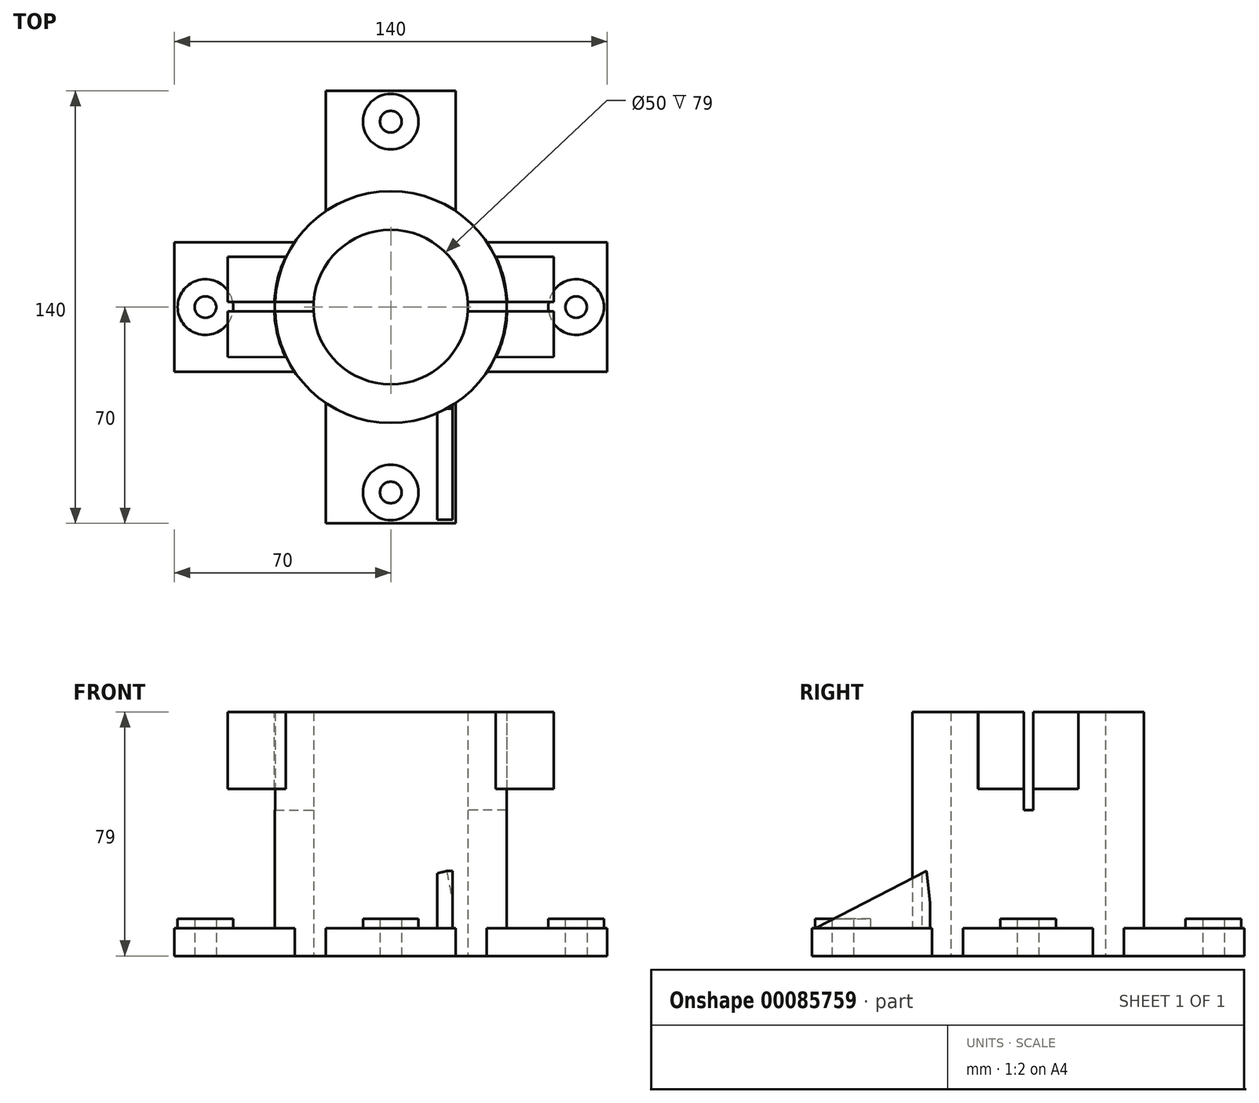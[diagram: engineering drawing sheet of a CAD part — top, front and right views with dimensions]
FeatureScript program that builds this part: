
annotation { "Feature Type Name" : "Feature", "Feature Type Description" : "" }
export const myFeature = defineFeature(function(context is Context, id is Id, definition is map)
    precondition{}
    {
        {
            var Q0;
            Q0=qCreatedBy(makeId("Top.planeOp"),FACE);
            var sketch = newSketch(context, id + "F0", { "sketchPlane" : qUnion([Q0])});
            skCircle(sketch, "E0", {"center": v(0, 0) * mm, "radius": 25 * mm});
            skCircle(sketch, "E1", {"center": v(0, 0) * mm, "radius": 37.5 * mm});
            skSolve(sketch);
        }
        {
            var Q0;
            Q0 = qSketchRegion(id + "F0", true);
            extrude(context, id + "F1", {"entities" : qUnion([Q0]), "depth" : 79 * mm});
        }
        {
            var Q0;
            Q0=qCreatedBy(makeId("Top.planeOp"),FACE);
            var sketch = newSketch(context, id + "F2", { "sketchPlane" : qUnion([Q0])});
            skLineSegment(sketch, "E2", {"start": v(-21, 31.07) * mm, "end": v(-21, 70) * mm});
            skLineSegment(sketch, "E3", {"start": v(21, 31.07) * mm, "end": v(21, 70) * mm});
            skArc(sketch, "E4", {"start": v(-21, 31.07) * mm, "mid": v(0, 37.5) * mm, "end": v(21, 31.07) * mm});
            skLineSegment(sketch, "E5", {"start": v(-21, 70) * mm, "end": v(21, 70) * mm});
            skPoint(sketch, "E6.center", {"position": v(0, -1.43) * mm});
            skLineSegment(sketch, "E7.1.0", {"start": v(-31.07, -21) * mm, "end": v(-70, -21) * mm});
            skLineSegment(sketch, "E7.1.1", {"start": v(-70, -21) * mm, "end": v(-70, 21) * mm});
            skLineSegment(sketch, "E7.1.2", {"start": v(-31.07, 21) * mm, "end": v(-70, 21) * mm});
            skArc(sketch, "E7.1.3", {"start": v(-31.07, -21) * mm, "mid": v(-37.5, 0) * mm, "end": v(-31.07, 21) * mm});
            skLineSegment(sketch, "E7.2.0", {"start": v(21, -31.07) * mm, "end": v(21, -70) * mm});
            skLineSegment(sketch, "E7.2.1", {"start": v(21, -70) * mm, "end": v(-21, -70) * mm});
            skLineSegment(sketch, "E7.2.2", {"start": v(-21, -31.07) * mm, "end": v(-21, -70) * mm});
            skArc(sketch, "E7.2.3", {"start": v(21, -31.07) * mm, "mid": v(0, -37.5) * mm, "end": v(-21, -31.07) * mm});
            skLineSegment(sketch, "E7.3.0", {"start": v(31.07, 21) * mm, "end": v(70, 21) * mm});
            skLineSegment(sketch, "E7.3.1", {"start": v(70, 21) * mm, "end": v(70, -21) * mm});
            skLineSegment(sketch, "E7.3.2", {"start": v(31.07, -21) * mm, "end": v(70, -21) * mm});
            skArc(sketch, "E7.3.3", {"start": v(31.07, 21) * mm, "mid": v(37.5, 0) * mm, "end": v(31.07, -21) * mm});
            skSolve(sketch);
        }
        {
            var Q0;
            Q0 = qSketchRegion(id + "F2", true);
            extrude(context, id + "F3", {"entities" : qUnion([Q0]), "operationType" : NewBodyOperationType.ADD, "depth" : 9 * mm});
        }
        {
            var Q0;
            Q0=qCreatedBy(makeId("Top.planeOp"),FACE);
            var sketch = newSketch(context, id + "F4", { "sketchPlane" : qUnion([Q0])});
            skCircle(sketch, "E8", {"center": v(-60, 0) * mm, "radius": 4 * mm});
            skCircle(sketch, "E9.1.0", {"center": v(0, -60) * mm, "radius": 4 * mm});
            skCircle(sketch, "E9.2.0", {"center": v(60, 0) * mm, "radius": 4 * mm});
            skCircle(sketch, "E9.3.0", {"center": v(0, 60) * mm, "radius": 4 * mm});
            skPoint(sketch, "E9.center", {"position": v(0, 0) * mm});
            skSolve(sketch);
        }
        {
            var Q0;
            Q0 = qSketchRegion(id + "F4", true);
            extrude(context, id + "F5", {"entities" : qUnion([Q0]), "operationType" : NewBodyOperationType.REMOVE, "depth" : 10 * mm});
        }
        {
            var Q0;
            Q0 = qSketchRegion(id + "F4", true);
            extrude(context, id + "F6", {"entities" : qUnion([Q0]), "operationType" : NewBodyOperationType.REMOVE, "depth" : 25 * mm});
        }
        {
            var Q0;
            Q0=qCreatedBy(makeId("Top.planeOp"),FACE);
            var sketch = newSketch(context, id + "F7", { "sketchPlane" : qUnion([Q0])});
            skCircle(sketch, "E10", {"center": v(-60, 0) * mm, "radius": 9 * mm});
            skCircle(sketch, "E11.1.0", {"center": v(0, -60) * mm, "radius": 9 * mm});
            skCircle(sketch, "E11.2.0", {"center": v(60, 0) * mm, "radius": 9 * mm});
            skCircle(sketch, "E11.3.0", {"center": v(0, 60) * mm, "radius": 9 * mm});
            skPoint(sketch, "E11.center", {"position": v(0, 0) * mm});
            skCircle(sketch, "E12", {"center": v(-60, 0) * mm, "radius": 3.5 * mm});
            skCircle(sketch, "E13.1.0", {"center": v(0, -60) * mm, "radius": 3.5 * mm});
            skCircle(sketch, "E13.2.0", {"center": v(60, 0) * mm, "radius": 3.5 * mm});
            skCircle(sketch, "E13.3.0", {"center": v(0, 60) * mm, "radius": 3.5 * mm});
            skSolve(sketch);
        }
        {
            var Q0;
            Q0 = qSketchRegion(id + "F7", true);
            extrude(context, id + "F8", {"entities" : qUnion([Q0]), "operationType" : NewBodyOperationType.ADD, "depth" : 12 * mm});
        }
        {
            var Q0;
            Q0=qCreatedBy(makeId("Right.planeOp"),FACE);
            var sketch = newSketch(context, id + "F9", { "sketchPlane" : qUnion([Q0])});
            skLineSegment(sketch, "E14.bottom", {"start": v(-1.35, 82.14) * mm, "end": v(1.65, 82.14) * mm});
            skLineSegment(sketch, "E14.top", {"start": v(-1.35, 47.14) * mm, "end": v(1.65, 47.14) * mm});
            skLineSegment(sketch, "E14.left", {"start": v(-1.35, 82.14) * mm, "end": v(-1.35, 47.14) * mm});
            skLineSegment(sketch, "E14.right", {"start": v(1.65, 82.14) * mm, "end": v(1.65, 47.14) * mm});
            skSolve(sketch);
        }
        {
            var Q0;
            Q0=qCreatedBy(makeId("Top.planeOp"),FACE);
            cPlane(context, id + "F10", {"entities" : qUnion([Q0]), "cplaneType" : CPlaneType.OFFSET, "offset" : 79 * mm, "width" : 150 * mm, "height" : 150 * mm});
        }
        {
            var Q0;
            Q0=qCreatedBy(id+"F10.planeOp",FACE);
            var sketch = newSketch(context, id + "F11", { "sketchPlane" : qUnion([Q0])});
            skArc(sketch, "E15", {"start": v(34.02, 16.28) * mm, "mid": v(37.72, 0) * mm, "end": v(34.02, -16.28) * mm});
            skLineSegment(sketch, "E16", {"start": v(34.02, 16.28) * mm, "end": v(52.8, 16.28) * mm});
            skLineSegment(sketch, "E17", {"start": v(52.8, 16.28) * mm, "end": v(52.8, -16.06) * mm});
            skLineSegment(sketch, "E18", {"start": v(52.8, -16.06) * mm, "end": v(34.02, -16.28) * mm});
            skLineSegment(sketch, "E19.MirrorCS", {"start": v(-34.02, 16.28) * mm, "end": v(-52.8, 16.28) * mm});
            skLineSegment(sketch, "E20.MirrorCS", {"start": v(-52.8, 16.28) * mm, "end": v(-52.8, -16.06) * mm});
            skLineSegment(sketch, "E21.MirrorCS", {"start": v(-52.8, -16.06) * mm, "end": v(-34.02, -16.28) * mm});
            skArc(sketch, "E22.MirrorCS", {"start": v(-34.02, 16.28) * mm, "mid": v(-37.72, 0) * mm, "end": v(-34.02, -16.28) * mm});
            skSolve(sketch);
        }
        {
            var Q0;
            Q0 = qSketchRegion(id + "F11", true);
            extrude(context, id + "F12", {"entities" : qUnion([Q0]), "oppositeDirection" : true, "depth" : 25 * mm});
        }
        {
            var Q0;
            Q0 = qSketchRegion(id + "F9", true);
            extrude(context, id + "F13", {"entities" : qUnion([Q0]), "operationType" : NewBodyOperationType.REMOVE, "endBound" : BoundingType.THROUGH_ALL, "oppositeDirection" : true, "depth" : 25 * mm});
        }
        {
            var Q0;
            Q0 = qSketchRegion(id + "F9", true);
            extrude(context, id + "F14", {"entities" : qUnion([Q0]), "operationType" : NewBodyOperationType.REMOVE, "endBound" : BoundingType.THROUGH_ALL, "depth" : 25 * mm});
        }
        {
            var Q0;
            Q0=qCreatedBy(makeId("Right.planeOp"),FACE);
            cPlane(context, id + "F15", {"entities" : qUnion([Q0]), "cplaneType" : CPlaneType.OFFSET, "offset" : 15 * mm, "width" : 150 * mm, "height" : 150 * mm});
        }
        {
            var Q0;
            Q0=qCreatedBy(id+"F15.planeOp",FACE);
            var sketch = newSketch(context, id + "F16", { "sketchPlane" : qUnion([Q0])});
            skLineSegment(sketch, "E23", {"start": v(-32.86, 27.5) * mm, "end": v(-69.3, 8.74) * mm});
            skLineSegment(sketch, "E24", {"start": v(-69.3, 8.74) * mm, "end": v(-30.78, 8.74) * mm});
            skLineSegment(sketch, "E25", {"start": v(-32.86, 27.5) * mm, "end": v(-30.78, 8.74) * mm});
            skSolve(sketch);
        }
        {
            var Q0;
            Q0 = qSketchRegion(id + "F16", true);
            extrude(context, id + "F17", {"entities" : qUnion([Q0]), "operationType" : NewBodyOperationType.ADD, "depth" : 5 * mm});
        }
    });
